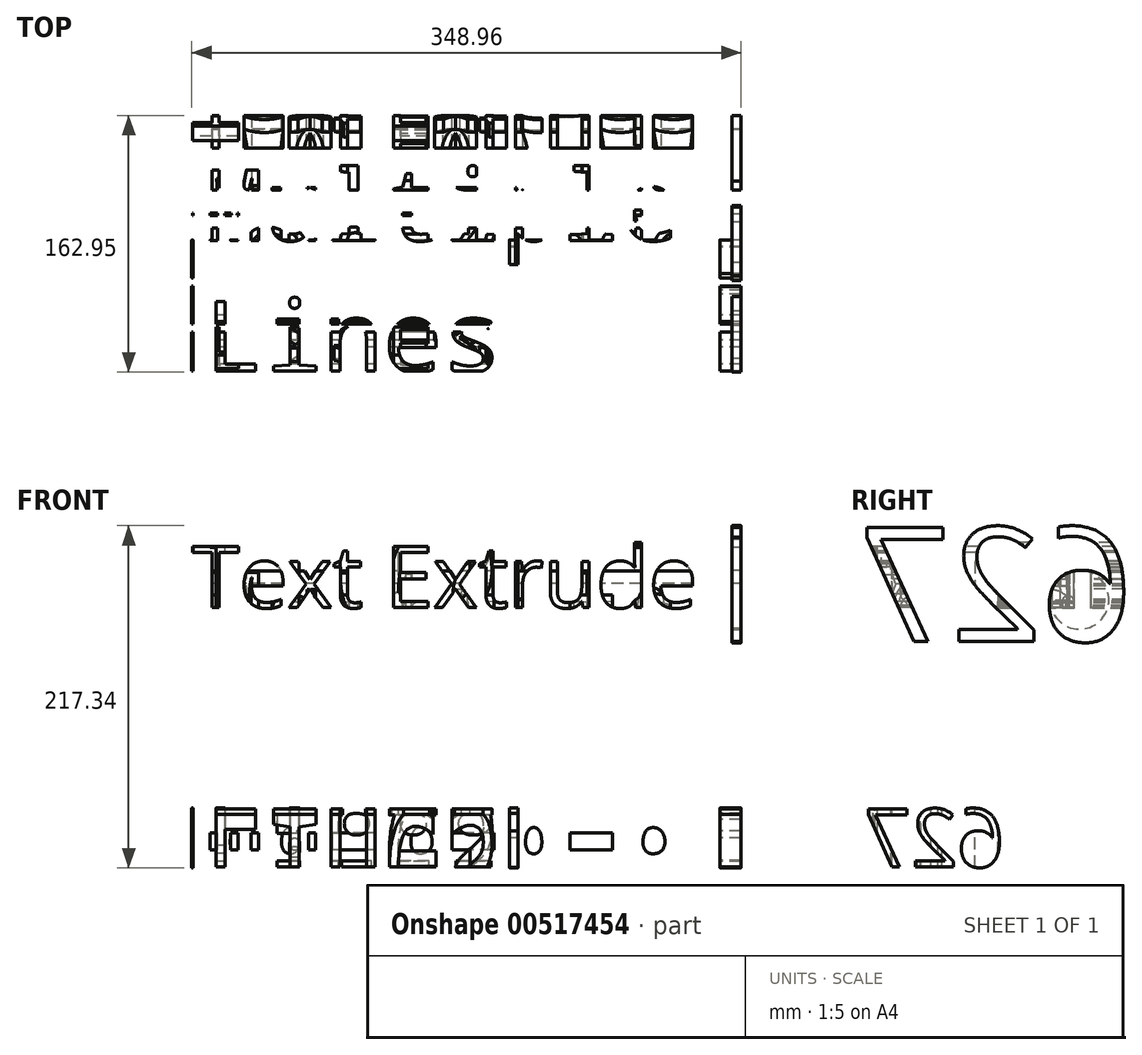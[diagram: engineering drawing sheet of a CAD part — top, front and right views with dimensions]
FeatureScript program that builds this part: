
annotation { "Feature Type Name" : "Feature", "Feature Type Description" : "" }
export const myFeature = defineFeature(function(context is Context, id is Id, definition is map)
    precondition{}
    {
        {
            var Q0;
            Q0=qCreatedBy(makeId("Front.planeOp"),FACE);
            var sketch = newSketch(context, id + "F0", { "sketchPlane" : qUnion([Q0])});
            skLineSegment(sketch, "E0.bottom", {"start": v(174.48, 187.08) * mm, "end": v(-174.48, 187.08) * mm});
            skLineSegment(sketch, "E0.top", {"start": v(174.48, -187.08) * mm, "end": v(-174.48, -187.08) * mm});
            skLineSegment(sketch, "E0.left", {"start": v(174.48, 187.08) * mm, "end": v(174.48, -187.08) * mm});
            skLineSegment(sketch, "E0.right", {"start": v(-174.48, 187.08) * mm, "end": v(-174.48, -187.08) * mm});
            skPoint(sketch, "E0.middle", {"position": v(0, 0) * mm});
            skSolve(sketch);
        }
        {
            var Q0;
            Q0=makeQuery(id+"F0.imprint","IMPRINT",FACE,{"disambiguationData":[TD([[makeQuery(id+"F0.imprint","IMPRINT",EDGE,{"derivedFrom":sQuery(id+"F0.wireOp",EDGE,"E0.bottom")}),1.0]])]});
            extrude(context, id + "F1", {"entities" : qUnion([Q0]), "depth" : 304.8 * mm, "offsetDistance" : 25.4 * mm});
        }
        {
            var Q0;
            Q0=makeQuery(id+"F1.opExtrude","CAP_FACE",FACE,{"disambiguationData":[OSD([sQuery(id+"F0.wireOp",EDGE,"E0.bottom"),sQuery(id+"F0.wireOp",EDGE,"E0.top"),sQuery(id+"F0.wireOp",EDGE,"E0.left"),sQuery(id+"F0.wireOp",EDGE,"E0.right")])],"isStart":false});
            var sketch = newSketch(context, id + "F2", { "sketchPlane" : qUnion([Q0])});
            skText(sketch, "E1", { "text": "Text Extrude", "fontName": "OpenSans-Regular.ttf"});
            const initialGuessF2  = {"E1": [-0.17448, 0, 1, 0, 0.0393]};
            skSetInitialGuess(sketch, initialGuessF2);
            skSolve(sketch);
        }
        {
            var Q0;
            Q0=makeQuery(id+"F1.opExtrude","SWEPT_FACE",FACE,{"disambiguationData":[OSD([sQuery(id+"F0.wireOp",EDGE,"E0.right")])]});
            var sketch = newSketch(context, id + "F3", { "sketchPlane" : qUnion([Q0])});
            skText(sketch, "E2", { "text": "627", "fontName": "OpenSans-Regular.ttf"});
            skText(sketch, "E3", { "text": "627", "fontName": "OpenSans-Regular.ttf"});
            const initialGuessF3  = {"E2": [0.09106, -0.16474, 1, 0, 0.03727], "E3": [0.00926, -0.02132, 1, 0, 0.073]};
            skSetInitialGuess(sketch, initialGuessF3);
            skSolve(sketch);
        }
        {
            var Q0;
            Q0=makeQuery(id+"F1.opExtrude","SWEPT_FACE",FACE,{"disambiguationData":[OSD([sQuery(id+"F0.wireOp",EDGE,"E0.bottom")])]});
            var sketch = newSketch(context, id + "F4", { "sketchPlane" : qUnion([Q0])});
            skText(sketch, "E4", { "text": "Multiple\nLines", "fontName": "DroidSansMono.ttf"});
            const initialGuessF4  = {"E4": [-0.16624, -0.0944, 1, 0, 0.04526]};
            skSetInitialGuess(sketch, initialGuessF4);
            skSolve(sketch);
        }
        {
            var Q0;
            Q0=makeQuery(id+"F2.imprint","IMPRINT",FACE,{"disambiguationData":[TD([[makeQuery(id+"F2.imprint","IMPRINT",EDGE,{"derivedFrom":sQuery(id+"F2.wireOp",EDGE,"E1.sketch_text.stroke-0")}),1.0]])]});
            var sketch = newSketch(context, id + "F5", { "sketchPlane" : qUnion([Q0])});
            skLineSegment(sketch, "E5.bottom", {"start": v(168.7, 90.46) * mm, "end": v(-178.94, 90.46) * mm});
            skLineSegment(sketch, "E5.top", {"start": v(168.7, -67.14) * mm, "end": v(-178.94, -67.14) * mm});
            skLineSegment(sketch, "E5.left", {"start": v(168.7, 90.46) * mm, "end": v(168.7, -67.14) * mm});
            skLineSegment(sketch, "E5.right", {"start": v(-178.94, 90.46) * mm, "end": v(-178.94, -67.14) * mm});
            skSolve(sketch);
        }
        {
            var Q0;
            Q0=makeQuery(id+"F4.imprint","IMPRINT",FACE,{"disambiguationData":[TD([[makeQuery(id+"F4.imprint","IMPRINT",EDGE,{"derivedFrom":sQuery(id+"F4.wireOp",EDGE,"E4.sketch_text.stroke-0")}),1.0]])]});
            var sketch = newSketch(context, id + "F6", { "sketchPlane" : qUnion([Q0])});
            skLineSegment(sketch, "E6.bottom", {"start": v(160.95, -206.36) * mm, "end": v(-173.62, -206.36) * mm});
            skLineSegment(sketch, "E6.top", {"start": v(160.95, -35.82) * mm, "end": v(-173.62, -35.82) * mm});
            skLineSegment(sketch, "E6.left", {"start": v(160.95, -206.36) * mm, "end": v(160.95, -35.82) * mm});
            skLineSegment(sketch, "E6.right", {"start": v(-173.62, -206.36) * mm, "end": v(-173.62, -35.82) * mm});
            skSolve(sketch);
        }
        {
            var Q0;
            Q0=makeQuery(id+"F6.imprint","IMPRINT",FACE,{"disambiguationData":[TD([[makeQuery(id+"F6.imprint","IMPRINT",EDGE,{"derivedFrom":sQuery(id+"F6.wireOp",EDGE,"E6.bottom")}),-1.0]])]});
            extrude(context, id + "F7", {"entities" : qUnion([Q0]), "operationType" : NewBodyOperationType.REMOVE, "oppositeDirection" : true, "depth" : 457.2 * mm, "offsetDistance" : 25.4 * mm});
        }
        {
            var Q0;
            {var subQ0=sQuery(id+"F5.wireOp",EDGE,"E5.left");Q0=makeQuery(id+"F5.imprint","IMPRINT",FACE,{"disambiguationData":[TD([[makeQuery(id+"F5.imprint","IMPRINT",EDGE,{"derivedFrom":subQ0}),-1.0]])]});}
            extrude(context, id + "F8", {"entities" : qUnion([Q0]), "operationType" : NewBodyOperationType.REMOVE, "oppositeDirection" : true, "depth" : 381 * mm, "offsetDistance" : 25.4 * mm});
        }
        {
            var Q0;
            Q0=makeQuery(id+"F3.imprint","IMPRINT",FACE,{"disambiguationData":[TD([[makeQuery(id+"F3.imprint","IMPRINT",EDGE,{"derivedFrom":sQuery(id+"F3.wireOp",EDGE,"E2.sketch_text.stroke-0")}),1.0]])]});
            extrude(context, id + "F9", {"entities" : qUnion([Q0]), "operationType" : NewBodyOperationType.REMOVE, "oppositeDirection" : true, "depth" : 381 * mm, "offsetDistance" : 25.4 * mm});
        }
    });
